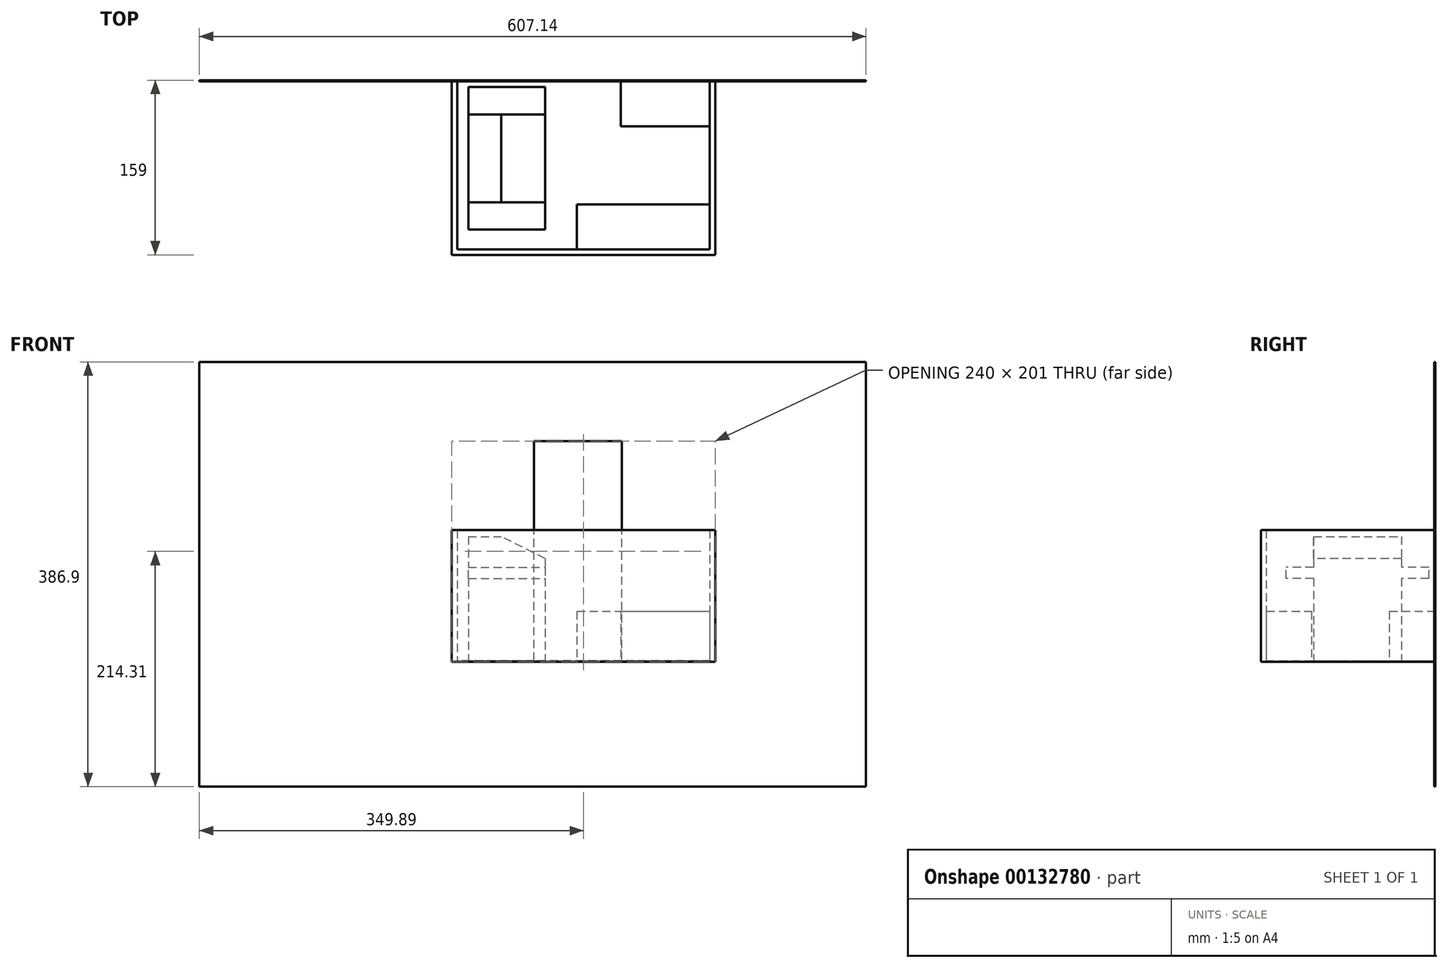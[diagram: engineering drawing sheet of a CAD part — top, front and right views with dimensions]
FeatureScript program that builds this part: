
annotation { "Feature Type Name" : "Feature", "Feature Type Description" : "" }
export const myFeature = defineFeature(function(context is Context, id is Id, definition is map)
    precondition{}
    {
        {
            var Q0;
            Q0=qCreatedBy(makeId("Top.planeOp"),FACE);
            var sketch = newSketch(context, id + "F0", { "sketchPlane" : qUnion([Q0])});
            skLineSegment(sketch, "E0.bottom", {"start": v(0, 0) * mm, "end": v(-230, 0) * mm});
            skLineSegment(sketch, "E0.top", {"start": v(0, 153) * mm, "end": v(-230, 153) * mm});
            skLineSegment(sketch, "E0.left", {"start": v(0, 0) * mm, "end": v(0, 153) * mm});
            skLineSegment(sketch, "E0.right", {"start": v(-230, 0) * mm, "end": v(-230, 153) * mm});
            skSolve(sketch);
        }
        {
            var Q0;
            Q0=makeQuery(id+"F0.imprint","IMPRINT",FACE,{"disambiguationData":[TD([[makeQuery(id+"F0.imprint","IMPRINT",EDGE,{"derivedFrom":sQuery(id+"F0.wireOp",EDGE,"E0.bottom")}),-1.0]])]});
            extrude(context, id + "F1", {"entities" : qUnion([Q0]), "depth" : 1 * mm});
        }
        {
            var Q0;
            Q0=makeQuery(id+"F1.opExtrude","CAP_FACE",FACE,{"disambiguationData":[OSD([sQuery(id+"F0.wireOp",EDGE,"E0.bottom"),sQuery(id+"F0.wireOp",EDGE,"E0.top"),sQuery(id+"F0.wireOp",EDGE,"E0.left"),sQuery(id+"F0.wireOp",EDGE,"E0.right")])],"isStart":true});
            var sketch = newSketch(context, id + "F2", { "sketchPlane" : qUnion([Q0])});
            skLineSegment(sketch, "E1.0.0", {"start": v(-230, 0) * mm, "end": v(0, 0) * mm});
            skLineSegment(sketch, "E1.0.1", {"start": v(0, 0) * mm, "end": v(0, -153) * mm});
            skLineSegment(sketch, "E1.0.2", {"start": v(0, -153) * mm, "end": v(-230, -153) * mm});
            skLineSegment(sketch, "E1.0.3", {"start": v(-230, -153) * mm, "end": v(-230, 0) * mm});
            skLineSegment(sketch, "E2.0", {"start": v(5, 5) * mm, "end": v(5, -153) * mm});
            skLineSegment(sketch, "E2.1", {"start": v(-235, 5) * mm, "end": v(5, 5) * mm});
            skLineSegment(sketch, "E2.2", {"start": v(-235, -153) * mm, "end": v(-235, 5) * mm});
            skLineSegment(sketch, "E3", {"start": v(-235, -153) * mm, "end": v(-230, -153) * mm});
            skLineSegment(sketch, "E4", {"start": v(0, -153) * mm, "end": v(5, -153) * mm});
            skSolve(sketch);
        }
        {
            var Q0;
            Q0=makeQuery(id+"F2.imprint","IMPRINT",FACE,{"disambiguationData":[TD([[makeQuery(id+"F2.imprint","IMPRINT",EDGE,{"derivedFrom":sQuery(id+"F2.wireOp",EDGE,"E1.0.0")}),-1.0]])]});
            extrude(context, id + "F3", {"entities" : qUnion([Q0]), "operationType" : NewBodyOperationType.ADD, "oppositeDirection" : true, "depth" : 120 * mm});
        }
        {
            var Q0;
            Q0=makeQuery(id+"F3.boolean.opBoolean","MERGE",FACE,{"derivedFrom":[makeQuery(id+"F1.opExtrude","SWEPT_FACE",FACE,{"disambiguationData":[OSD([sQuery(id+"F0.wireOp",EDGE,"E0.top")])]}),makeQuery(id+"F3.opExtrude","SWEPT_FACE",FACE,{"disambiguationData":[OSD([sQuery(id+"F2.wireOp",EDGE,"E3")])]}),makeQuery(id+"F3.opExtrude","SWEPT_FACE",FACE,{"disambiguationData":[OSD([sQuery(id+"F2.wireOp",EDGE,"E4")])]})]});
            var sketch = newSketch(context, id + "F4", { "sketchPlane" : qUnion([Q0])});
            skLineSegment(sketch, "E5.bottom", {"start": v(-142.25, 273.1) * mm, "end": v(464.89, 273.1) * mm});
            skLineSegment(sketch, "E5.top", {"start": v(-142.25, -113.8) * mm, "end": v(464.89, -113.8) * mm});
            skLineSegment(sketch, "E5.left", {"start": v(-142.25, 273.1) * mm, "end": v(-142.25, -113.8) * mm});
            skLineSegment(sketch, "E5.right", {"start": v(464.89, 273.1) * mm, "end": v(464.89, -113.8) * mm});
            skLineSegment(sketch, "E6.0", {"start": v(0, 1) * mm, "end": v(230, 1) * mm});
            skLineSegment(sketch, "E7.bottom", {"start": v(160, 1) * mm, "end": v(80, 1) * mm});
            skLineSegment(sketch, "E7.top", {"start": v(160, 201) * mm, "end": v(80, 201) * mm});
            skLineSegment(sketch, "E7.left", {"start": v(160, 1) * mm, "end": v(160, 201) * mm});
            skLineSegment(sketch, "E7.right", {"start": v(80, 1) * mm, "end": v(80, 201) * mm});
            skSolve(sketch);
        }
        {
            var Q0;
            Q0=makeQuery(id+"F4.imprint","IMPRINT",FACE,{"disambiguationData":[TD([[makeQuery(id+"F4.imprint","IMPRINT",EDGE,{"derivedFrom":sQuery(id+"F4.wireOp",EDGE,"E5.bottom")}),-1.0]])]});
            var Q1;
            {var subQ5=sQuery(id+"F4.wireOp",EDGE,"E7.bottom");Q1=makeQuery(id+"F4.imprint","IMPRINT",FACE,{"disambiguationData":[TD([[makeQuery(id+"F4.imprint","IMPRINT",EDGE,{"derivedFrom":subQ5}),-1.0]])]});}
            extrude(context, id + "F5", {"entities" : qUnion([Q0, Q1]), "operationType" : NewBodyOperationType.ADD, "depth" : 1 * mm});
        }
        {
            var Q0;
            Q0=makeQuery(id+"F1.opExtrude","CAP_FACE",FACE,{"disambiguationData":[OSD([sQuery(id+"F0.wireOp",EDGE,"E0.bottom"),sQuery(id+"F0.wireOp",EDGE,"E0.top"),sQuery(id+"F0.wireOp",EDGE,"E0.left"),sQuery(id+"F0.wireOp",EDGE,"E0.right")])],"isStart":false});
            var sketch = newSketch(context, id + "F6", { "sketchPlane" : qUnion([Q0])});
            skLineSegment(sketch, "E8.bottom", {"start": v(-121, 0) * mm, "end": v(0, 0) * mm});
            skLineSegment(sketch, "E8.top", {"start": v(-121, 41) * mm, "end": v(0, 41) * mm});
            skLineSegment(sketch, "E8.left", {"start": v(-121, 0) * mm, "end": v(-121, 41) * mm});
            skLineSegment(sketch, "E8.right", {"start": v(0, 0) * mm, "end": v(0, 41) * mm});
            skLineSegment(sketch, "E9.bottom", {"start": v(-81, 153) * mm, "end": v(0, 153) * mm});
            skLineSegment(sketch, "E9.top", {"start": v(-81, 112) * mm, "end": v(0, 112) * mm});
            skLineSegment(sketch, "E9.left", {"start": v(-81, 153) * mm, "end": v(-81, 112) * mm});
            skLineSegment(sketch, "E9.right", {"start": v(0, 153) * mm, "end": v(0, 112) * mm});
            skLineSegment(sketch, "E10.bottom", {"start": v(-41, 112) * mm, "end": v(0, 112) * mm});
            skLineSegment(sketch, "E10.top", {"start": v(-41, 41) * mm, "end": v(0, 41) * mm});
            skLineSegment(sketch, "E10.left", {"start": v(-41, 112) * mm, "end": v(-41, 41) * mm});
            skLineSegment(sketch, "E10.right", {"start": v(0, 112) * mm, "end": v(0, 41) * mm});
            skSolve(sketch);
        }
        {
            var Q0;
            Q0=makeQuery(id+"F6.imprint","IMPRINT",FACE,{"disambiguationData":[TD([[makeQuery(id+"F6.imprint","IMPRINT",EDGE,{"derivedFrom":sQuery(id+"F6.wireOp",EDGE,"E9.bottom")}),1.0]])]});
            var Q1;
            Q1=makeQuery(id+"F6.imprint","IMPRINT",FACE,{"disambiguationData":[TD([[makeQuery(id+"F6.imprint","IMPRINT",EDGE,{"derivedFrom":sQuery(id+"F6.wireOp",EDGE,"E10.bottom")}),-1.0]])]});
            var Q2;
            Q2=makeQuery(id+"F6.imprint","IMPRINT",FACE,{"disambiguationData":[TD([[makeQuery(id+"F6.imprint","IMPRINT",EDGE,{"derivedFrom":sQuery(id+"F6.wireOp",EDGE,"E8.bottom")}),-1.0]])]});
            extrude(context, id + "F7", {"entities" : qUnion([Q0, Q1, Q2]), "depth" : 45 * mm});
        }
        {
            var Q0;
            Q0=makeQuery(id+"F1.opExtrude","CAP_FACE",FACE,{"disambiguationData":[OSD([sQuery(id+"F0.wireOp",EDGE,"E0.bottom"),sQuery(id+"F0.wireOp",EDGE,"E0.top"),sQuery(id+"F0.wireOp",EDGE,"E0.left"),sQuery(id+"F0.wireOp",EDGE,"E0.right")])],"isStart":false});
            var sketch = newSketch(context, id + "F8", { "sketchPlane" : qUnion([Q0])});
            skLineSegment(sketch, "E11.bottom", {"start": v(-220, 43) * mm, "end": v(-150, 43) * mm});
            skLineSegment(sketch, "E11.top", {"start": v(-220, 123) * mm, "end": v(-150, 123) * mm});
            skLineSegment(sketch, "E11.left", {"start": v(-220, 43) * mm, "end": v(-220, 123) * mm});
            skLineSegment(sketch, "E11.right", {"start": v(-150, 43) * mm, "end": v(-150, 123) * mm});
            skSolve(sketch);
        }
        {
            var Q0;
            Q0=makeQuery(id+"F8.imprint","IMPRINT",FACE,{"disambiguationData":[TD([[makeQuery(id+"F8.imprint","IMPRINT",EDGE,{"derivedFrom":sQuery(id+"F8.wireOp",EDGE,"E11.bottom")}),1.0]])]});
            extrude(context, id + "F9", {"entities" : qUnion([Q0]), "depth" : 113 * mm});
        }
        {
            var Q0;
            Q0=makeQuery(id+"F9.opExtrude","SWEPT_FACE",FACE,{"disambiguationData":[OSD([sQuery(id+"F8.wireOp",EDGE,"E11.top")])]});
            cPlane(context, id + "F10", {"entities" : qUnion([Q0]), "cplaneType" : CPlaneType.OFFSET, "offset" : 40 * mm, "oppositeDirection" : true, "width" : 150 * mm, "height" : 150 * mm});
        }
        {
            var Q0;
            Q0=qCreatedBy(id+"F10.planeOp",FACE);
            var sketch = newSketch(context, id + "F11", { "sketchPlane" : qUnion([Q0])});
            skLineSegment(sketch, "E12.0.0", {"start": v(150, 1) * mm, "end": v(220, 1) * mm});
            skLineSegment(sketch, "E12.0.1", {"start": v(220, 1) * mm, "end": v(220, 114) * mm});
            skLineSegment(sketch, "E12.0.2", {"start": v(220, 114) * mm, "end": v(150, 114) * mm});
            skLineSegment(sketch, "E12.0.3", {"start": v(150, 114) * mm, "end": v(150, 1) * mm});
            skLineSegment(sketch, "E13.bottom", {"start": v(150, 86) * mm, "end": v(220, 86) * mm});
            skLineSegment(sketch, "E13.top", {"start": v(150, 76) * mm, "end": v(220, 76) * mm});
            skLineSegment(sketch, "E13.left", {"start": v(150, 86) * mm, "end": v(150, 76) * mm});
            skLineSegment(sketch, "E13.right", {"start": v(220, 86) * mm, "end": v(220, 76) * mm});
            skSolve(sketch);
        }
        {
            var Q0;
            Q0=makeQuery(id+"F11.imprint","IMPRINT",FACE,{"disambiguationData":[TD([[makeQuery(id+"F11.imprint","IMPRINT",EDGE,{"derivedFrom":sQuery(id+"F11.wireOp",EDGE,"E13.bottom")}),-1.0]])]});
            extrude(context, id + "F12", {"entities" : qUnion([Q0]), "operationType" : NewBodyOperationType.ADD, "endBound" : BoundingType.SYMMETRIC, "depth" : 130 * mm});
        }
        {
            var Q0;
            Q0=makeQuery(id+"F9.opExtrude","CAP_EDGE",EDGE,{"disambiguationData":[OSD([sQuery(id+"F8.wireOp",EDGE,"E11.right")])],"isStart":false});
            chamfer(context, id + "F13", {"entities" : qUnion([Q0]), "chamferType" : ChamferType.TWO_OFFSETS, "width1" : 40 * mm, "oppositeDirection" : false, "width2" : 20 * mm, "tangentPropagation" : true});
        }
    });
